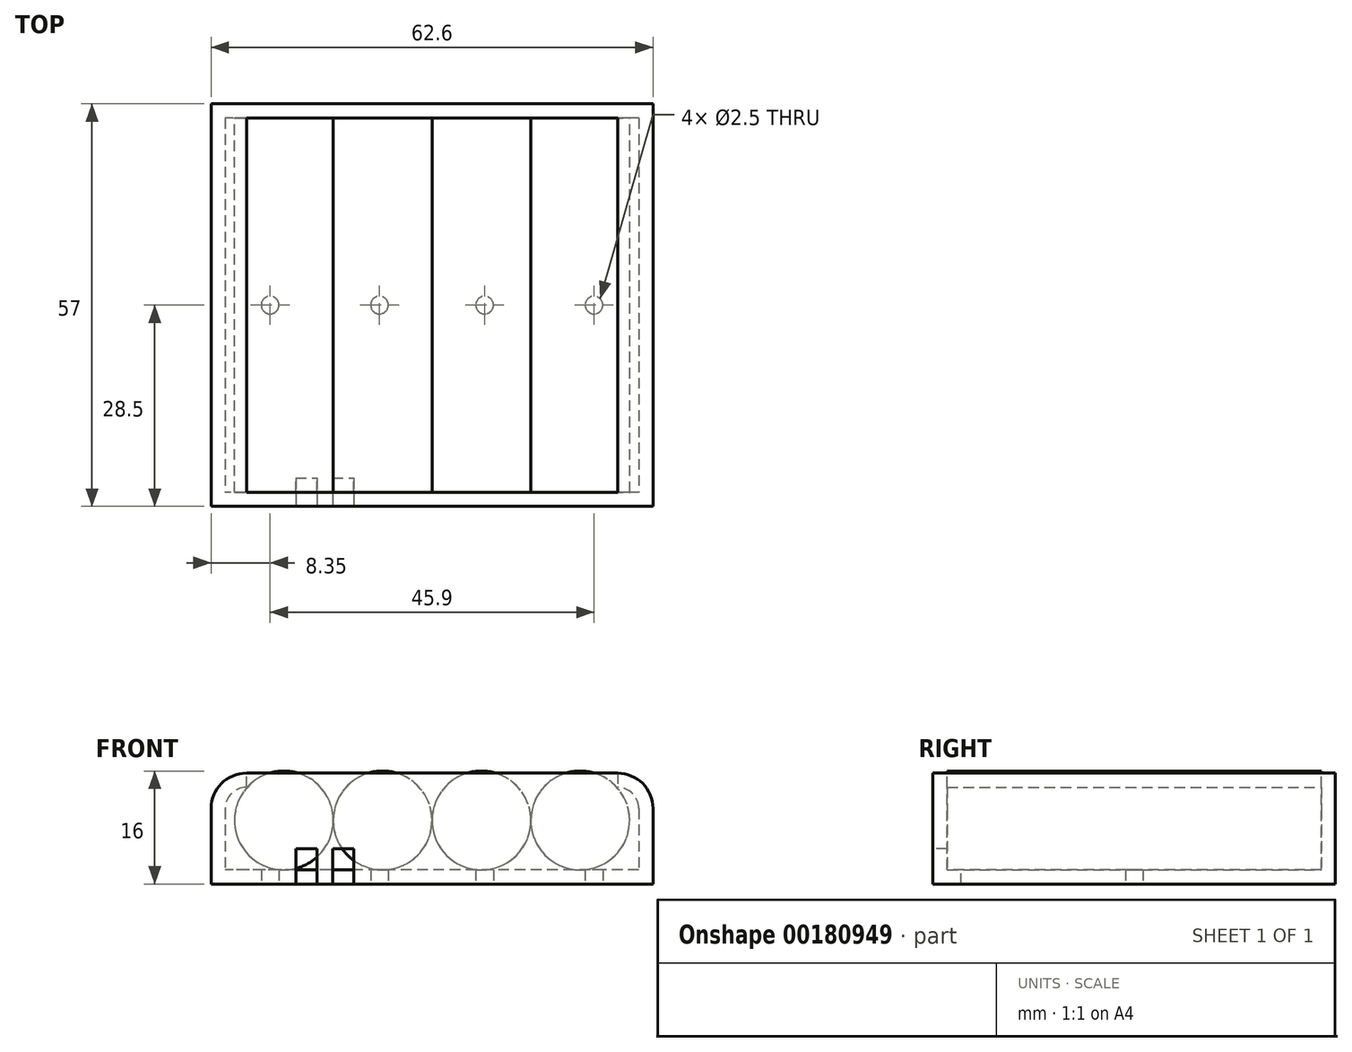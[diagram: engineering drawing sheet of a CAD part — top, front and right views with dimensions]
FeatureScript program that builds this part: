
annotation { "Feature Type Name" : "Feature", "Feature Type Description" : "" }
export const myFeature = defineFeature(function(context is Context, id is Id, definition is map)
    precondition{}
    {
        {
            var Q0;
            Q0=qCreatedBy(makeId("Top.planeOp"),FACE);
            var sketch = newSketch(context, id + "F0", { "sketchPlane" : qUnion([Q0])});
            skLineSegment(sketch, "E0.bottom", {"start": v(31.3, 28.5) * mm, "end": v(-31.3, 28.5) * mm});
            skLineSegment(sketch, "E0.top", {"start": v(31.3, -28.5) * mm, "end": v(-31.3, -28.5) * mm});
            skLineSegment(sketch, "E0.left", {"start": v(31.3, 28.5) * mm, "end": v(31.3, -28.5) * mm});
            skLineSegment(sketch, "E0.right", {"start": v(-31.3, 28.5) * mm, "end": v(-31.3, -28.5) * mm});
            skPoint(sketch, "E0.middle", {"position": v(0, 0) * mm});
            skSolve(sketch);
        }
        {
            var Q0;
            Q0 = qSketchRegion(id + "F0", true);
            extrude(context, id + "F1", {"entities" : qUnion([Q0]), "depth" : 15.7 * mm, "offsetDistance" : 25 * mm});
        }
        {
            var Q0;
            Q0=makeQuery(id+"F1.opExtrude","CAP_EDGE",EDGE,{"disambiguationData":[OSD([sQuery(id+"F0.wireOp",EDGE,"E0.right")])],"isStart":false});
            var Q1;
            Q1=makeQuery(id+"F1.opExtrude","CAP_EDGE",EDGE,{"disambiguationData":[OSD([sQuery(id+"F0.wireOp",EDGE,"E0.left")])],"isStart":false});
            fillet(context, id + "F2", {"entities" : qUnion([Q0, Q1]), "radius" : 5 * mm, "tangentPropagation" : true, "allowEdgeOverflow" : false});
        }
        {
            var Q0;
            Q0=makeQuery(id+"F1.opExtrude","CAP_FACE",FACE,{"disambiguationData":[OSD([sQuery(id+"F0.wireOp",EDGE,"E0.bottom"),sQuery(id+"F0.wireOp",EDGE,"E0.top"),sQuery(id+"F0.wireOp",EDGE,"E0.left"),sQuery(id+"F0.wireOp",EDGE,"E0.right")])],"isStart":false});
            shell(context, id + "F3", {"entities" : qUnion([Q0]), "thickness" : 2 * mm});
        }
        {
            var Q0;
            Q0=makeQuery(id+"F1.opExtrude","SWEPT_FACE",FACE,{"disambiguationData":[OSD([sQuery(id+"F0.wireOp",EDGE,"E0.top")])]});
            var sketch = newSketch(context, id + "F4", { "sketchPlane" : qUnion([Q0])});
            skLineSegment(sketch, "E1.bottom", {"start": v(-19.3, 0) * mm, "end": v(-16.3, 0) * mm});
            skLineSegment(sketch, "E1.top", {"start": v(-19.3, 5) * mm, "end": v(-16.3, 5) * mm});
            skLineSegment(sketch, "E1.left", {"start": v(-19.3, 0) * mm, "end": v(-19.3, 5) * mm});
            skLineSegment(sketch, "E1.right", {"start": v(-16.3, 0) * mm, "end": v(-16.3, 5) * mm});
            skLineSegment(sketch, "E2.bottom", {"start": v(-14.1, 0) * mm, "end": v(-11.1, 0) * mm});
            skLineSegment(sketch, "E2.top", {"start": v(-14.1, 5) * mm, "end": v(-11.1, 5) * mm});
            skLineSegment(sketch, "E2.left", {"start": v(-14.1, 0) * mm, "end": v(-14.1, 5) * mm});
            skLineSegment(sketch, "E2.right", {"start": v(-11.1, 0) * mm, "end": v(-11.1, 5) * mm});
            skSolve(sketch);
        }
        {
            var Q0;
            Q0 = qSketchRegion(id + "F4", true);
            extrude(context, id + "F5", {"entities" : qUnion([Q0]), "operationType" : NewBodyOperationType.REMOVE, "oppositeDirection" : true, "depth" : 4 * mm, "offsetDistance" : 25 * mm});
        }
        {
            var Q0;
            Q0=makeQuery(id+"F1.opExtrude","CAP_FACE",FACE,{"disambiguationData":[OSD([sQuery(id+"F0.wireOp",EDGE,"E0.bottom"),sQuery(id+"F0.wireOp",EDGE,"E0.top"),sQuery(id+"F0.wireOp",EDGE,"E0.left"),sQuery(id+"F0.wireOp",EDGE,"E0.right")])],"isStart":true});
            var sketch = newSketch(context, id + "F6", { "sketchPlane" : qUnion([Q0])});
            skCircle(sketch, "E3", {"center": v(-22.95, 0) * mm, "radius": 1.25 * mm});
            skCircle(sketch, "E4.MirrorC", {"center": v(22.95, 0) * mm, "radius": 1.25 * mm});
            skCircle(sketch, "E5", {"center": v(-7.45, 0) * mm, "radius": 1.25 * mm});
            skCircle(sketch, "E6.MirrorC", {"center": v(7.45, 0) * mm, "radius": 1.25 * mm});
            skSolve(sketch);
        }
        {
            var Q0;
            Q0 = qSketchRegion(id + "F6", true);
            extrude(context, id + "F7", {"entities" : qUnion([Q0]), "operationType" : NewBodyOperationType.REMOVE, "oppositeDirection" : true, "depth" : 25 * mm, "offsetDistance" : 25 * mm});
        }
        {
            var Q0;
            Q0=makeQuery(id+"F3.opShell","OFFSET_FACE",FACE,{"disambiguationData":[OSD([sQuery(id+"F0.wireOp",EDGE,"E0.bottom")])]});
            var sketch = newSketch(context, id + "F8", { "sketchPlane" : qUnion([Q0])});
            skCircle(sketch, "E7", {"center": v(21, 9) * mm, "radius": 7 * mm});
            skCircle(sketch, "E8", {"center": v(7, 9) * mm, "radius": 7 * mm});
            skCircle(sketch, "E9.MirrorC", {"center": v(-21, 9) * mm, "radius": 7 * mm});
            skCircle(sketch, "E10.MirrorC", {"center": v(-7, 9) * mm, "radius": 7 * mm});
            skSolve(sketch);
        }
        {
            var Q0;
            Q0 = qSketchRegion(id + "F8", true);
            var Q1;
            Q1=makeQuery(id+"F3.opShell","OFFSET_FACE",FACE,{"disambiguationData":[OSD([sQuery(id+"F0.wireOp",EDGE,"E0.top")])]});
            extrude(context, id + "F9", {"entities" : qUnion([Q0]), "endBound" : BoundingType.UP_TO_SURFACE, "depth" : 25 * mm, "endBoundEntityFace" : qUnion([Q1]), "offsetDistance" : 25 * mm});
        }
    });
